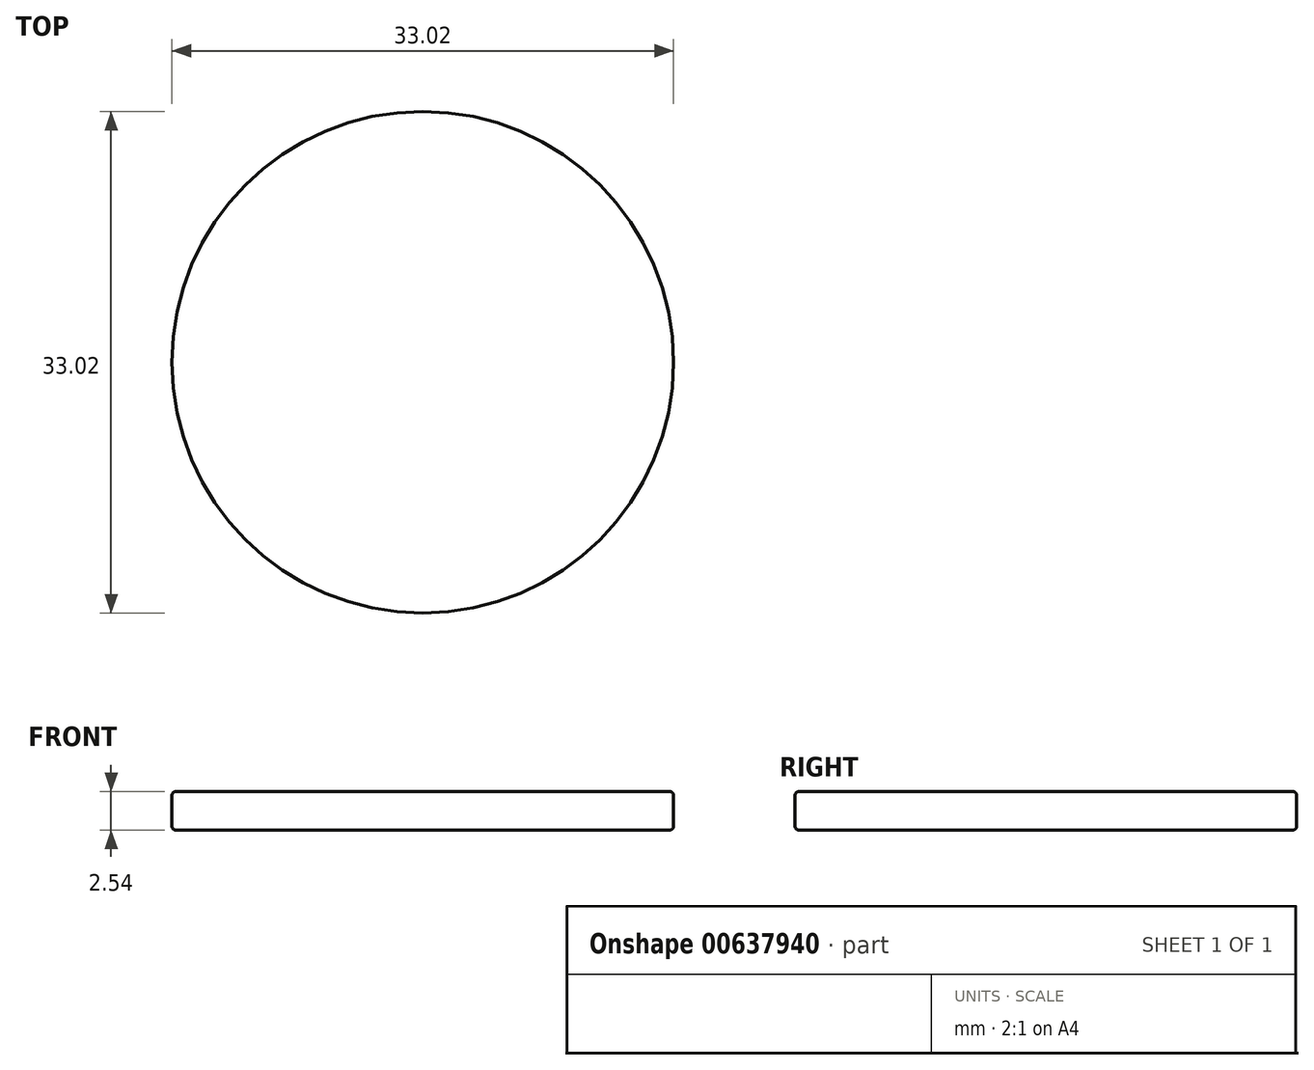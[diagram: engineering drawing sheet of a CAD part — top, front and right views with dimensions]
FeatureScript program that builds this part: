
annotation { "Feature Type Name" : "Feature", "Feature Type Description" : "" }
export const myFeature = defineFeature(function(context is Context, id is Id, definition is map)
    precondition{}
    {
        {
            var Q0;
            Q0=qCreatedBy(makeId("Top.planeOp"),FACE);
            var sketch = newSketch(context, id + "F0", { "sketchPlane" : qUnion([Q0])});
            skCircle(sketch, "E0", {"center": v(0, 0) * mm, "radius": 16.51 * mm});
            skSolve(sketch);
        }
        {
            var Q0;
            Q0 = qSketchRegion(id + "F0", true);
            extrude(context, id + "F1", {"entities" : qUnion([Q0]), "endBound" : BoundingType.SYMMETRIC, "depth" : 2.54 * mm, "offsetDistance" : 25.4 * mm});
        }
        {
            var Q0;
            Q0=makeQuery(id+"F1.opExtrude","CAP_EDGE",EDGE,{"disambiguationData":[OSD([sQuery(id+"F0.wireOp",EDGE,"E0")])],"isStart":false});
            var Q1;
            Q1=makeQuery(id+"F1.opExtrude","CAP_EDGE",EDGE,{"disambiguationData":[OSD([sQuery(id+"F0.wireOp",EDGE,"E0")])],"isStart":true});
            fillet(context, id + "F2", {"entities" : qUnion([Q0, Q1]), "radius" : 0.25 * mm, "tangentPropagation" : true, "allowEdgeOverflow" : false});
        }
    });
